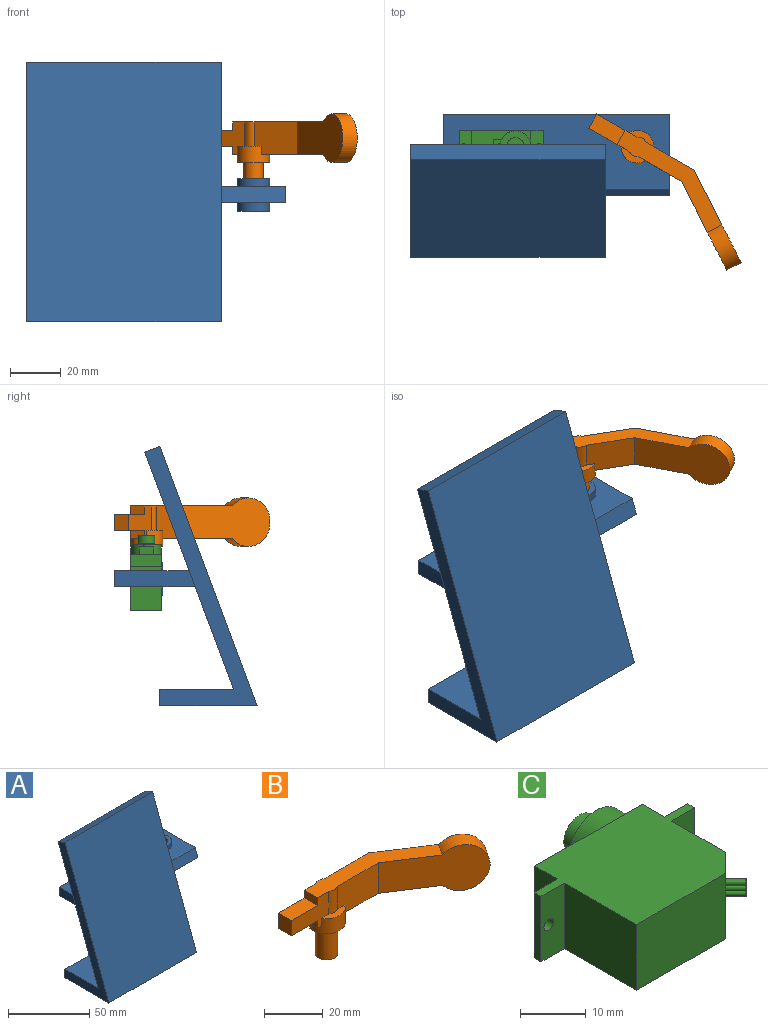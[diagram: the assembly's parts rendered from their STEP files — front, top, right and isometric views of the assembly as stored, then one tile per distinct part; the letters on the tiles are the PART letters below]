
ASSEMBLY  parts=3 mates=4
PART A: 23 faces, bbox 101.6x56x101.6 mm
  f0: plane 93.02x76.2mm, normal (0,0.94,-0.35), area 7139.5mm2, adj f2,f3,f6,f7,f8,f10,f11
  f1: plane 76.2x6.35mm, normal (0,1,0), area 483.9mm2, adj f2,f5,f6,f7
  f2: plane 76.2x28.94mm, normal (0,0,1), area 2205mm2, adj f0,f1,f6,f7
  f3: plane 76.2x5.95mm, normal (0,0.35,0.94), area 483.9mm2, adj f0,f4,f6,f7
  f4: plane 101.6x76.2mm, normal (0,-0.94,0.35), area 8268.4mm2, adj f3,f5,f6,f7
  f5: plane 76.2x38.1mm, normal (0,0,-1), area 2903.2mm2, adj f1,f4,f6,f7
  f6: plane 101.6x44.05mm, normal (1,0,0), area 872.8mm2, adj f0,f1,f2,f3,f4,f5,f12
  f7: plane 101.6x44.05mm, normal (-1,0,0), area 872.8mm2, adj f0,f1,f2,f3,f4,f5
  f8: plane 88.9x31.75mm, normal (0,0,-1), area 2377.2mm2, adj f0,f9,f11,f12,f13,f17,f19,f20
  f9: plane 88.9x6.35mm, normal (0,1,0), area 564.5mm2, adj f8,f10,f11,f13
  f10: plane 88.9x29.37mm, normal (0,0,1), area 2165.5mm2, adj f0,f9,f11,f12,f13,f15,f19,f20
  f11: plane 31.75x6.35mm, normal (-1,0,0), area 194.1mm2, adj f0,f8,f9,f10
  f12: plane 25.4x6.35mm, normal (0,-0.94,0.35), area 172.3mm2, adj f6,f8,f10,f13
  f13: plane 31.75x6.35mm, normal (1,0,0), area 194.1mm2, adj f8,f9,f10,f12
  f14: cylinder r=3.94mm len=12.7mm, axis (0,0,1), area 314.2mm2, adj f16,f18
  f15: cylinder r=6.35mm len=12.7mm, axis (0,0,-1), area 126.7mm2, adj f10,f16
  f16: plane 12.7x12.7mm, normal (0,0,1), area 78mm2, adj f14,f15
  f17: cylinder r=6.35mm len=12.7mm, axis (0,0,1), area 126.7mm2, adj f8,f18
  f18: plane 12.7x12.7mm, normal (0,0,-1), area 78mm2, adj f14,f17
  f19: plane 13.21x6.35mm, normal (1,0,0), area 83.9mm2, adj f8,f10,f20,f22
  f20: plane 24.13x6.35mm, normal (0,1,0), area 153.2mm2, adj f8,f10,f19,f21
  f21: plane 13.21x6.35mm, normal (-1,0,0), area 83.9mm2, adj f8,f10,f20,f22
  f22: plane 24.13x6.35mm, normal (0,-1,0), area 153.2mm2, adj f8,f10,f19,f21
PART B: 23 faces, bbox 78.2x30.7x31.8 mm
  f0: plane 6.35x6.35mm, normal (-1,0,0), area 40.3mm2, adj f1,f4,f20,f22
  f1: plane 18.1x12.7mm, normal (0,-1,0), area 138.4mm2, adj f0,f2,f3,f7,f8,f17,f19,f20
  f2: plane 6.35x2mm, normal (0,0,-1), area 9.1mm2, adj f1,f4,f8,f19
  f3: plane 51.51x19.14mm, normal (0,0,1), area 343.5mm2, adj f1,f4,f11,f12,f14,f15,f16,f17
  f4: plane 18.1x12.7mm, normal (0,1,0), area 138.4mm2, adj f0,f2,f3,f8,f10,f16,f19,f20
  f5: cylinder r=3.81mm len=12.7mm, axis (0,0,-1), area 304mm2, adj f6,f9
  f6: plane 7.62x7.62mm, normal (0,0,-1), area 45.6mm2, adj f5
  f7: plane 11x3.18mm, normal (0,0,1), area 23mm2, adj f1,f8,f15,f17
  f8: cylinder r=6.35mm len=12.7mm, axis (0,0,1), area 211.1mm2, adj f1,f2,f4,f7,f9,f10,f13,f14
  f9: plane 12.7x12.7mm, normal (0,0,-1), area 81.1mm2, adj f5,f8
  f10: plane 11x3.18mm, normal (0,0,1), area 23mm2, adj f4,f8,f14,f16
  f11: plane 32.74x21.19mm, normal (-0.54,-0.84,0), area 548mm2, adj f3,f13,f15,f18
  f12: plane 34.32x22.2mm, normal (0.54,0.84,0), area 571.9mm2, adj f3,f13,f14,f18
  f13: plane 38.51x18.5mm, normal (0,0,-1), area 253.7mm2, adj f8,f11,f12,f14,f15,f18
  f14: plane 21.55x12.7mm, normal (0,1,0), area 262.9mm2, adj f3,f8,f10,f12,f13,f16
  f15: plane 19.67x12.7mm, normal (0,-1,0), area 239mm2, adj f3,f7,f8,f11,f13,f17
  f16: cylinder r=3.81mm len=9.53mm, axis (0,0,-1), area 42.5mm2, adj f3,f4,f10,f14
  f17: cylinder r=3.81mm len=9.53mm, axis (0,0,-1), area 42.5mm2, adj f1,f3,f7,f15
  f18: cylinder r=9.53mm len=19.05mm, axis (-0.54,-0.84,0), area 291.8mm2, adj f3,f11,f12,f13
  f19: plane 6.35x3.18mm, normal (-1,0,0), area 20.2mm2, adj f1,f2,f4,f20
  f20: plane 12.7x6.35mm, normal (0,0,-1), area 80.6mm2, adj f0,f1,f4,f19
  f21: plane 6.35x3.18mm, normal (-1,0,0), area 20.2mm2, adj f1,f3,f4,f22
  f22: plane 12.7x6.35mm, normal (0,0,1), area 80.6mm2, adj f0,f1,f4,f21
PART C: 37 faces, bbox 33x29.3x12.2 mm
  f0: cylinder r=0.5mm len=2.92mm, axis (-0.71,0.71,0), area 9.8mm2, adj f9,f33
  f1: cylinder r=0.5mm len=2.92mm, axis (-0.71,0.71,0), area 9.8mm2, adj f9,f32
  f2: cylinder r=0.5mm len=2.92mm, axis (-0.71,0.71,0), area 9.8mm2, adj f9,f31
  f3: cylinder r=3.35mm len=6.71mm, axis (0,1,0), area 66mm2, adj f29,f30
  f4: cylinder r=1.16mm len=2.32mm, axis (0,-1,0), area 3mm2, adj f7,f10,f25
  f5: cylinder r=1.03mm len=2.06mm, axis (0,1,0), area 9.7mm2, adj f22,f23
  f6: cylinder r=1.03mm len=2.06mm, axis (0,1,0), area 9.7mm2, adj f20,f21
  f7: cylinder r=6mm len=12mm, axis (0,-1,0), area 127.9mm2, adj f4,f10,f11,f25,f27,f28
  f8: cylinder r=2.34mm len=4.69mm, axis (0,-1,0), area 6.5mm2, adj f10,f29
  f9: plane 12.2x3.94mm, normal (0.71,-0.71,0), area 65.6mm2, adj f0,f1,f2,f15,f16,f17,f18
  f10: plane 13.16x12mm, normal (0,1,0), area 98mm2, adj f4,f7,f8
  f11: plane 23.06x12.2mm, normal (0,1,0), area 152.4mm2, adj f7,f12,f13,f17,f18,f26,f27,f28
  f12: plane 12.2x4.79mm, normal (-1,0,0), area 58.5mm2, adj f11,f17,f18,f22
  f13: plane 12.2x4.79mm, normal (1,0,0), area 58.5mm2, adj f11,f17,f18,f21
  f14: plane 15.54x12.2mm, normal (-1,0,0), area 189.5mm2, adj f16,f17,f18,f23
  f15: plane 12.2x11.6mm, normal (1,0,0), area 141.5mm2, adj f9,f17,f18,f20
  f16: plane 19.12x12.2mm, normal (0,-1,0), area 233.3mm2, adj f9,f14,f17,f18
  f17: plane 33x21.83mm, normal (0,0,-1), area 510.5mm2, adj f9,f11,f12,f13,f14,f15,f16,f19
  f18: plane 33x21.83mm, normal (0,0,1), area 510.5mm2, adj f9,f11,f12,f13,f14,f15,f16,f19
  f19: plane 12.2x1.5mm, normal (1,0,0), area 18.3mm2, adj f17,f18,f20,f21
  f20: plane 12.2x4.96mm, normal (0,-1,0), area 57.1mm2, adj f6,f15,f17,f18,f19
  f21: plane 12.2x4.96mm, normal (0,1,0), area 57.1mm2, adj f6,f13,f17,f18,f19
  f22: plane 12.2x4.98mm, normal (0,1,0), area 57.5mm2, adj f5,f12,f17,f18,f24
  f23: plane 12.2x4.98mm, normal (0,-1,0), area 57.5mm2, adj f5,f14,f17,f18,f24
  f24: plane 12.2x1.5mm, normal (-1,0,0), area 18.3mm2, adj f17,f18,f22,f23
  f25: plane 5.45x3.35mm, normal (0,1,0), area 13.7mm2, adj f4,f7,f26,f27,f28
  f26: plane 5.45x3.13mm, normal (-1,0,0), area 17.1mm2, adj f11,f25,f27,f28
  f27: plane 3.35x3.13mm, normal (0,0,1), area 10.5mm2, adj f7,f11,f25,f26
  f28: plane 3.35x3.13mm, normal (0,0,-1), area 10.5mm2, adj f7,f11,f25,f26
  f29: plane 6.71x6.71mm, normal (0,-1,0), area 18.1mm2, adj f3,f8
  f30: plane 6.71x6.71mm, normal (0,1,0), area 35.4mm2, adj f3
  f31: plane 1x0.71mm, normal (0.71,-0.71,0), area 0.8mm2, adj f2
  f32: plane 1x0.71mm, normal (0.71,-0.71,0), area 0.8mm2, adj f1
  f33: plane 1x0.71mm, normal (0.71,-0.71,0), area 0.8mm2, adj f0
  f34: cylinder r=0.64mm len=1.27mm, axis (0,1,0), area 3.2mm2, adj f35,f36
  f35: plane 1.27x1.27mm, normal (0,-1,0), area 1.3mm2, adj f34
  f36: plane 1.27x1.27mm, normal (0,1,0), area 1.3mm2, adj f34
PLACE A t=(55.73,44.46,-3.67)mm
PLACE B rot(axis=(0,0,-1),30deg) t=(106.53,49.64,61.89)mm
PLACE C rot(axis=(1,0,0),90deg) t=(41.6,43.79,33.66)mm
MATE planar A.f22 <-> C.f17  axis (0,-1,0) through (53.66,55.99,46.02)mm
MATE planar A.f19 <-> C.f14  axis (1,0,0) through (41.6,49.38,46.02)mm
MATE planar A.f10 <-> C.f20  axis (0,0,1) through (76.03,47.28,49.19)mm
MATE revolute B.f5 <-> A.f14  axis (0,0,-1) through (106.53,49.64,52.37)mm
